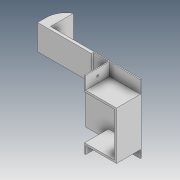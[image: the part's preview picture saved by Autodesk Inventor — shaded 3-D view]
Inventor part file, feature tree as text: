
AUTODESK INVENTOR PART (.ipt)
format: ipt  version: 2021 (Build 250183000, 183)  size: 200,192 bytes
history: native  units: in
note: dims shown in document units (in); Inventor stores cm internally (conversion verified against a paired STEP export)
features: extrude x11, sketch x11, other x1, fillet x1
ambient origin geometry x8: Origin, YZ Plane, XZ Plane, XY Plane, X Axis, Y Axis, Z Axis, Center Point
bodies: Body1 (feature_tree)
feature tree (24):
  other  "Sólido1"
  extrude  "Extrusão1"  Depth=1.9685in
  extrude  "Extrusão2"  Depth=0.252in
  extrude  "Extrusão3"  Depth=0.0197in
  extrude  "Extrusão4"  Depth=0.0197in TaperAngle=0.0deg
  extrude  "Extrusão5"  Depth=0.0197in TaperAngle=0.0deg
  extrude  "Extrusão6"  Depth=0.2913in
  extrude  "Extrusão7"  Depth=0.5906in
  extrude  "Extrusão8"  Depth=0.0394in
  extrude  "Extrusão9"  Depth=0.4724in TaperAngle=0.0deg
  fillet  "Arredondamento1"  Radius=0.0394in
  extrude  "Extrusão10"  Depth=0.4724in TaperAngle=0.0deg
  extrude  "Extrusão11"  Depth=0.4724in TaperAngle=0.0deg
  sketch  "Esboço1"  dims[d0=1.9685in d1=1.2362in]
  sketch  "Esboço2"  dims[d2=0.0197in d3=0.0in d4=0.252in]
  sketch  "Esboço3"  dims[d5=0.0197in d6=0.0in d7=1.1811in]
  sketch  "Esboço4"  dims[d8=0.1181in d9=0.0197in d10=0.0in]
  sketch  "Esboço5"  dims[d11=0.0394in d12=0.0197in d13=0.0in]
  sketch  "Esboço6"  dims[d14=0.1929in d15=0.2913in]
  sketch  "Esboço7"  dims[d16=0.5906in d17=0.5906in]
  sketch  "Esboço8"  dims[d18=0.0394in d19=0.0394in]
  sketch  "Esboço9"  dims[d20=0.0197in d21=0.4724in d22=0.0in d23=0.0394in]
  sketch  "Esboço10"  dims[d24=0.0197in d25=0.0in d26=0.4724in d27=0.0in]
  sketch  "Esboço11"  dims[d28=0.4528in d29=0.4724in d30=0.0in d31=0.1969in d32=0.4724in d33=0.0in d34=0.3937in d35=0.0394in d36=0.0in d37=1.063in d38=0.126in d39=0.0748in d40=0.0394in d41=0.0394in d42=0.0394in d43=0.0in]
